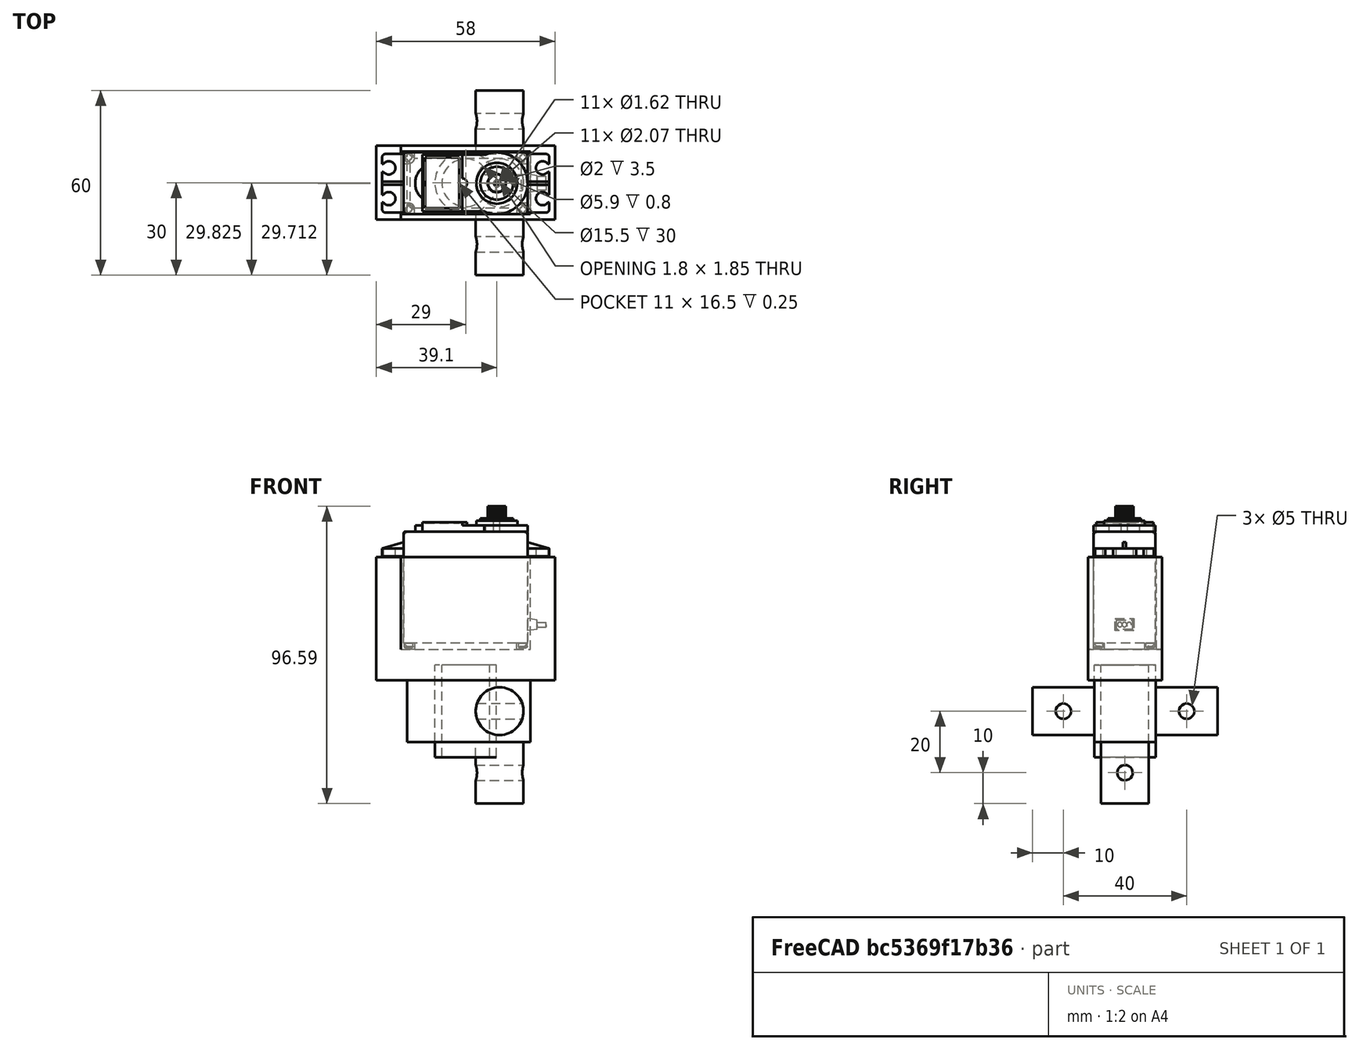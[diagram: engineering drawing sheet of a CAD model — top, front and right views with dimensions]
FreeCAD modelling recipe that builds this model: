
FCSTD DOCUMENT  (FreeCAD 0.21R33771 (Git))
Label: U_Servo_Rotativo_cuello_v0
License: All rights reserved
LicenseURL: http://en.wikipedia.org/wiki/All_rights_reserved
objects: Part::Cylinder×5, Mesh::Feature×2, Sketcher::SketchObject×2, PartDesign::Pad×2, Part::MultiFuse×2, Part::FeaturePython×1, Part::Feature×1, PartDesign::Body×1, Part::Box×1, Part::Cut×1
note: 18 computed .brp shape members not serialized (recipe doc carries the construction recipe); baked Part::Feature solids carry a one-line shape summary decoded from their .brp

FEATURE [Part::FeaturePython] Tube  # WARN: FeaturePython — macro-defined, semantics opaque (R4)
  AttacherType = Attacher::AttachEngine3D
  Height = 30
  InnerRadius = 7.75
  OuterRadius = 10
  Placement = pos=(0,-12,-37) rot=(0,0,1;0rad)
FEATURE [Mesh::Feature] servo_lower_cover_fake_shaft
FEATURE [Mesh::Feature] futaba  label="Servo"
  Placement = pos=(0,-3,2) rot=(0,0,1;0rad)
FEATURE [Part::Feature] Part__Feature  label="MG996R"
  Placement = pos=(0,-9,-0.5) rot=(0,0,1;0rad)
  shape: bbox 54.21 x 20.13 x 46.64 mm, 453 faces, 11 solids (baked)
FEATURE [Sketcher::SketchObject] Sketch
  FullyConstrained = false
  MapMode = 5
  Placement = pos=(0,0,0) rot=(1,0,0;1.5708rad)
  Support = -> [XZ_Plane]
  sketch-geometry (9):
    g0: LineSegment StartX=-21.001 StartY=28 StartZ=0 EndX=-29 EndY=28 EndZ=0
    g1: LineSegment StartX=-29 StartY=28 StartZ=0 EndX=-29 EndY=-2 EndZ=0
    g2: LineSegment StartX=21 StartY=28 StartZ=0 EndX=29 EndY=28 EndZ=0
    g3: LineSegment StartX=21 StartY=28 StartZ=0 EndX=21 EndY=-2 EndZ=0
    g4: LineSegment StartX=-21.001 StartY=28 StartZ=0 EndX=-21.001 EndY=-2 EndZ=0
    g5: LineSegment StartX=-29 StartY=-2 StartZ=0 EndX=-29 EndY=-12 EndZ=0
    g6: LineSegment StartX=-29 StartY=-12 StartZ=0 EndX=29 EndY=-12 EndZ=0
    g7: LineSegment StartX=29 StartY=28 StartZ=0 EndX=29 EndY=-12 EndZ=0
    g8: LineSegment StartX=-21.001 StartY=-2 StartZ=0 EndX=21 EndY=-2 EndZ=0
  constraints (18):
    c: Horizontal(g0)
    c: Coincident(g1,g0)
    c: Vertical(g1)
    c: Horizontal(g2)
    c: Coincident(g3,g2)
    c: Vertical(g3)
    c: Coincident(g4,g0)
    c: Vertical(g4)
    c: Coincident(g5,g1)
    c: Vertical(g5)
    c: Coincident(g6,g5)
    c: Horizontal(g6)
    c: Coincident(g7,g2)
    c: Coincident(g7,g6)
    c: Vertical(g7)
    c: Coincident(g8,g4)
    c: Coincident(g8,g3)
    c: Horizontal(g8)
FEATURE [PartDesign::Pad] Pad
  Direction = (0,-1,2e-16)
  Length = 24
  Length2 = 10
  Placement = pos=(0,0,0) rot=(1,0,0;1.5708rad)
  Profile = -> Sketch
  ReferenceAxis = -> Sketch [N_Axis]
  Type = 0
FEATURE [Sketcher::SketchObject] Sketch003
  FullyConstrained = false
  MapMode = 5
  Placement = pos=(0,0,-2) rot=(0,0,1;3.14159rad)
  sketch-geometry (8):
    g0: LineSegment StartX=21 StartY=1.8 StartZ=0 EndX=21 EndY=0 EndZ=0
    g1: LineSegment StartX=-21 StartY=0 StartZ=0 EndX=-21 EndY=1.8 EndZ=0
    g2: LineSegment StartX=21 StartY=24 StartZ=0 EndX=21 EndY=22.2 EndZ=0
    g3: LineSegment StartX=-21 StartY=22.2 StartZ=0 EndX=-21 EndY=24 EndZ=0
    g4: LineSegment StartX=-21 StartY=24 StartZ=0 EndX=21 EndY=24 EndZ=0
    g5: LineSegment StartX=21 StartY=22.2 StartZ=0 EndX=-21 EndY=22.2 EndZ=0
    g6: LineSegment StartX=-21 StartY=1.8 StartZ=0 EndX=21 EndY=1.8 EndZ=0
    g7: LineSegment StartX=21 StartY=0 StartZ=0 EndX=-21 EndY=0 EndZ=0
  constraints (17):
    c: Vertical(g0)
    c: Vertical(g1)
    c: PointOnObject(g0,g-1)
    c: Vertical(g2)
    c: Vertical(g3)
    c: Coincident(g4,g3)
    c: Coincident(g4,g2)
    c: Horizontal(g4)
    c: Coincident(g5,g2)
    c: Coincident(g5,g3)
    c: Horizontal(g5)
    c: Coincident(g6,g1)
    c: Coincident(g6,g0)
    c: Horizontal(g6)
    c: Coincident(g7,g0)
    c: Coincident(g7,g1)
    c: Horizontal(g7)
FEATURE [PartDesign::Pad] Pad002
  BaseFeature = -> Pad
  Direction = (0,2e-16,1)
  Length = 30
  Length2 = 10
  Placement = pos=(0,0,0) rot=(1,0,0;1.5708rad)
  Profile = -> Sketch003
  ReferenceAxis = -> Sketch003 [N_Axis]
  Type = 0
FEATURE [PartDesign::Body] Body  label="U Servo Bracket"
  Group = -> [Sketch,Pad,Sketch003,Pad002]
  Origin = -> Origin
  Tip = -> Pad002
FEATURE [Part::Box] Box001  label="Cubo001"
  AttacherType = Attacher::AttachEngine3D
  Height = 20
  Length = 20
  Placement = pos=(-10,-30,-10) rot=(0,0,1;0rad)
  Width = 40
FEATURE [Part::Cylinder] Cylinder015  label="Ligamento_cadera002"
  Angle = 360
  AttacherType = Attacher::AttachEngine3D
  FirstAngle = 0
  Height = 60
  Placement = pos=(-30,0,0) rot=(0,1,0;1.5708rad)
  Radius = 7.75
  SecondAngle = 0
FEATURE [Part::Cylinder] Cylinder016  label="Ligamento_cadera003"
  Angle = 360
  AttacherType = Attacher::AttachEngine3D
  FirstAngle = 0
  Height = 30
  Radius = 7.75
  SecondAngle = 0
FEATURE [Part::Cylinder] Cylinder017  label="Taladros003"
  Angle = 360
  AttacherType = Attacher::AttachEngine3D
  FirstAngle = 0
  Height = 30
  Placement = pos=(20,15,0) rot=(1,0,0;1.5708rad)
  Radius = 2.5
  SecondAngle = 0
FEATURE [Part::Cylinder] Cylinder018  label="Taladros004"
  Angle = 360
  AttacherType = Attacher::AttachEngine3D
  FirstAngle = 0
  Height = 30
  Placement = pos=(-20,15,0) rot=(1,0,0;1.5708rad)
  Radius = 2.5
  SecondAngle = 0
FEATURE [Part::Cylinder] Cylinder019  label="Taladros005"
  Angle = 360
  AttacherType = Attacher::AttachEngine3D
  FirstAngle = 0
  Height = 30
  Placement = pos=(0,15,20) rot=(1,0,0;1.5708rad)
  Radius = 2.5
  SecondAngle = 0
FEATURE [Part::MultiFuse] Fusion003  label="Ligamento_T001"
  Shapes = -> [Box001,Cylinder016,Cylinder015]
FEATURE [Part::MultiFuse] Fusion004  label="Taladros_ligamento_T001"
  Shapes = -> [Cylinder019,Cylinder017,Cylinder018]
FEATURE [Part::Cut] Cut001  label="Ligamento_T_imprimir001"
  Base = -> Fusion003
  Placement = pos=(11,-12,-22) rot=(0.707107,0.707107,0;3.14159rad)
  Tool = -> Fusion004
